# Revit family: Hager-Orion_Inox-IP65-D160-Cl.I-Inox_encl-630A-400mm-NoHosted-IT-it
name_source: partatom
category: Equipement électrique
units: mm (PartAtom-declared; Revit-internal decimal feet)

## family parameters
Basée sur le plan de construction = Oui
Configuration du panneau = Deux colonnes, circuits au sein
Cote de connecteur circulaire = Utiliser le diamètre
Couper avec des vides une fois chargée = Non
Partagée = Non
Point de calcul de pièce = Non
Toujours verticalement = Oui
Type d'élément = Tableau de raccordement

## types (2) — shared parameters
Commentaires du type = Orion Inox
EF000003 - Tipo di montaggio = EV001247 - apparente/incassato
EF000007 - colore = EV000154 - altri
EF000008 - Larghezza = 300 mm  [stored 0.984252 ft]
EF000040 - Altezza = 400 mm  [stored 1.31234 ft]
EF000049 - profondità = 160 mm  [stored 0.524934 ft]
EF000118 - con piastra di montaggio = Oui
EF000339 - tipo di copertura = EV004216 - porta
EF000437 - numero di ingressi per conduttori = 2
EF001088 - possibilità di applicazione = Non
EF001131 - profondità interna = 160 mm  [stored 0.524934 ft]
EF001596 - Attacco Lampada = EV000166 - acciaio inossidabile
EF003532 - adatto per uso esterno = Oui
EF004293 - resistenza agli urti = EV008784 - IK10
EF004464 - tipo di porta = EV002646 - singolo
EF005474 - grado di protezione (IP) = EV006421 - IP65
EF006244 - coperchio/porta trasparente = Non
EF006306 - con serratura = Oui
EF007800 - adatto per parafulmine = Non
EF008873 - corrente nominale (In) = 630 A
EF009170 - spessore materiale scatola = 1 mm  [stored 0.00328084 ft]
EF009171 - spessore materiale porta/coperchio = 2 mm  [stored 0.00656168 ft]
EF009212 - esecuzione coperchio = EV009916 - con taglio
EF009554 - numero delle aperture per la piastra della flangia = 2
EF015940 - Coprire con rilascio di sovrapressione = Non
Elévation par défaut = 1219 mm
Fabricant = Hager
HG000002 - Con porta = Oui
HG000003 - Gamma = Orion Inox
HG000004 - Codice produttore = FL706BW
HG000009 - Porta doppia a battente = Non
HG000010 - Porte asimmetriche = Non
HG000023 - Custodia a doppia sezione = Non
HG000024 - Altezza della sezione inferiore = 600 mm
HG000026 - A pavimento = Non
zero-valued in all types: EF000218 - profondità di incasso, EF000266 - numero di file, EF002950 - Numero moduli DIN, EF004427 - numero di moduli, HG000027 - Altezza dello zoccolo

## per-type parameters (varying)
| type | HG000006 - Ad incasso |
| apparente IP65 L300 A400 P160  - FL706BW | Non |
| incassato IP65 L300 A400 P160  - FL706BW | Oui |

note: [stored X ft] marks values corroborated as IEEE doubles in the binary element streams (Revit-internal decimal feet)

## geometry (parser evidence)
native form markers: Blend x4, Sweep x8
no freeform markers — native parametric forms only
